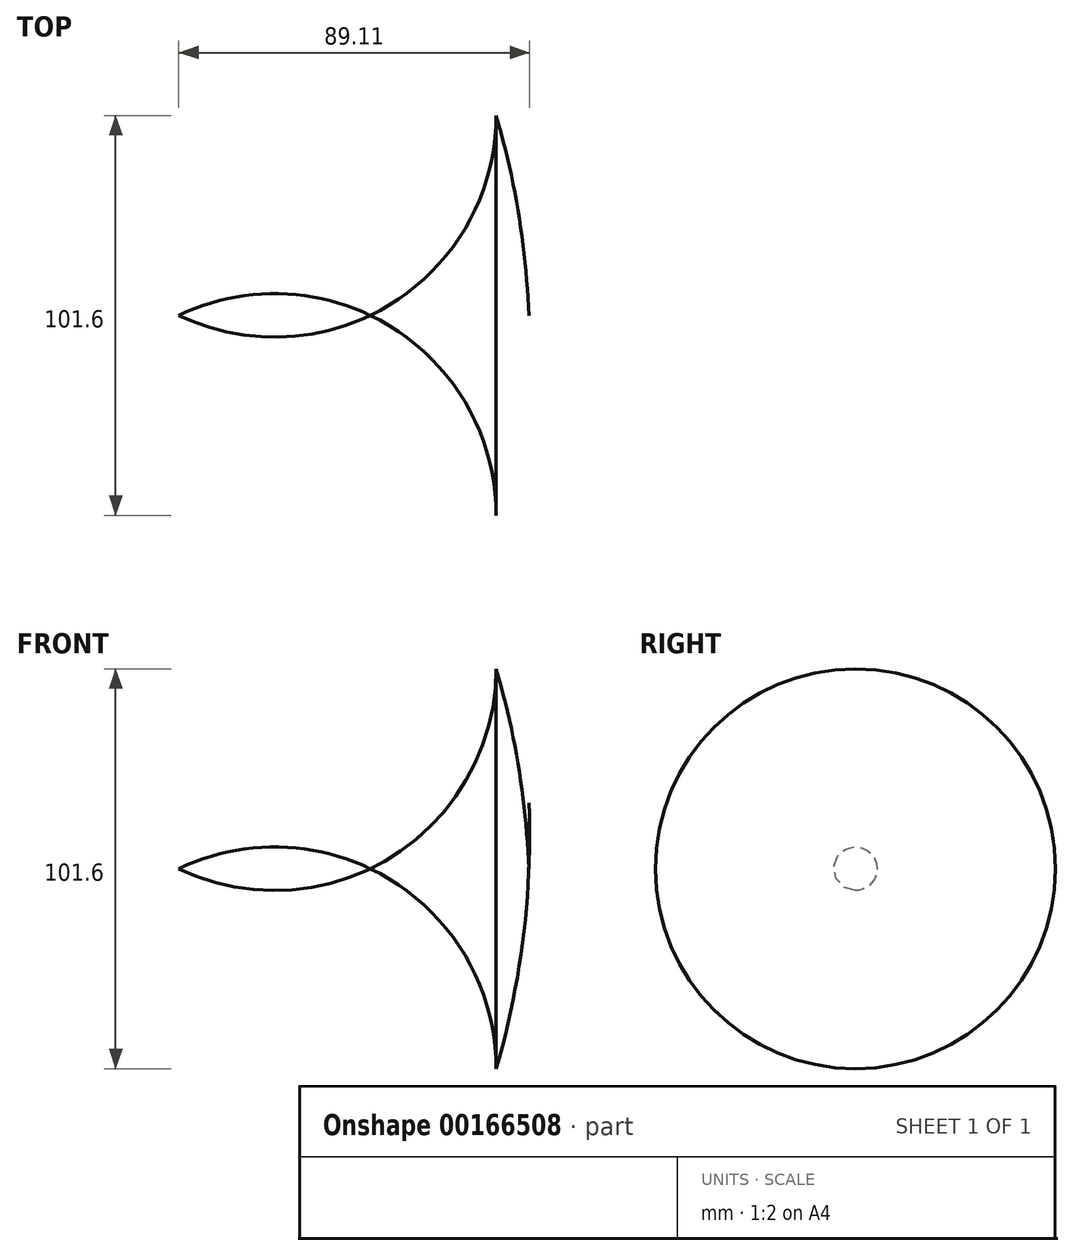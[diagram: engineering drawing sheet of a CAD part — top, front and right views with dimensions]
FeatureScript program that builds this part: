
annotation { "Feature Type Name" : "Feature", "Feature Type Description" : "" }
export const myFeature = defineFeature(function(context is Context, id is Id, definition is map)
    precondition{}
    {
        {
            var Q0;
            Q0=qCreatedBy(makeId("Top.planeOp"),FACE);
            var sketch = newSketch(context, id + "F0", { "sketchPlane" : qUnion([Q0])});
            skLineSegment(sketch, "E0", {"start": v(0, 0) * mm, "end": v(40.3, 0) * mm});
            skLineSegment(sketch, "E1", {"start": v(40.3, 0) * mm, "end": v(32, 0) * mm});
            skLineSegment(sketch, "E2", {"start": v(32, 0) * mm, "end": v(32, 50.8) * mm});
            skArc(sketch, "E3", {"start": v(0, 0) * mm, "mid": v(23.34, 20.78) * mm, "end": v(32, 50.8) * mm});
            skArc(sketch, "E4", {"start": v(40.3, 0) * mm, "mid": v(37.71, 25.65) * mm, "end": v(32, 50.8) * mm});
            skSolve(sketch);
        }
        {
            var Q0;
            Q0=makeQuery(id+"F0.imprint","IMPRINT",FACE,{"disambiguationData":[TD([[makeQuery(id+"F0.imprint","IMPRINT",EDGE,{"derivedFrom":sQuery(id+"F0.wireOp",EDGE,"E1")}),-1.0]])]});
            var Q1;
            Q1=makeQuery(id+"F0.imprint","IMPRINT",FACE,{"disambiguationData":[TD([[makeQuery(id+"F0.imprint","IMPRINT",EDGE,{"derivedFrom":sQuery(id+"F0.wireOp",EDGE,"E0")}),1.0]])]});
            var Q2;
            Q2=sQuery(id+"F0.wireOp",EDGE,"E0");
            revolve(context, id + "F1", {"entities" : qUnion([Q0, Q1]), "axis" : qUnion([Q2]), "revolveType" : RevolveType.FULL});
        }
    });
